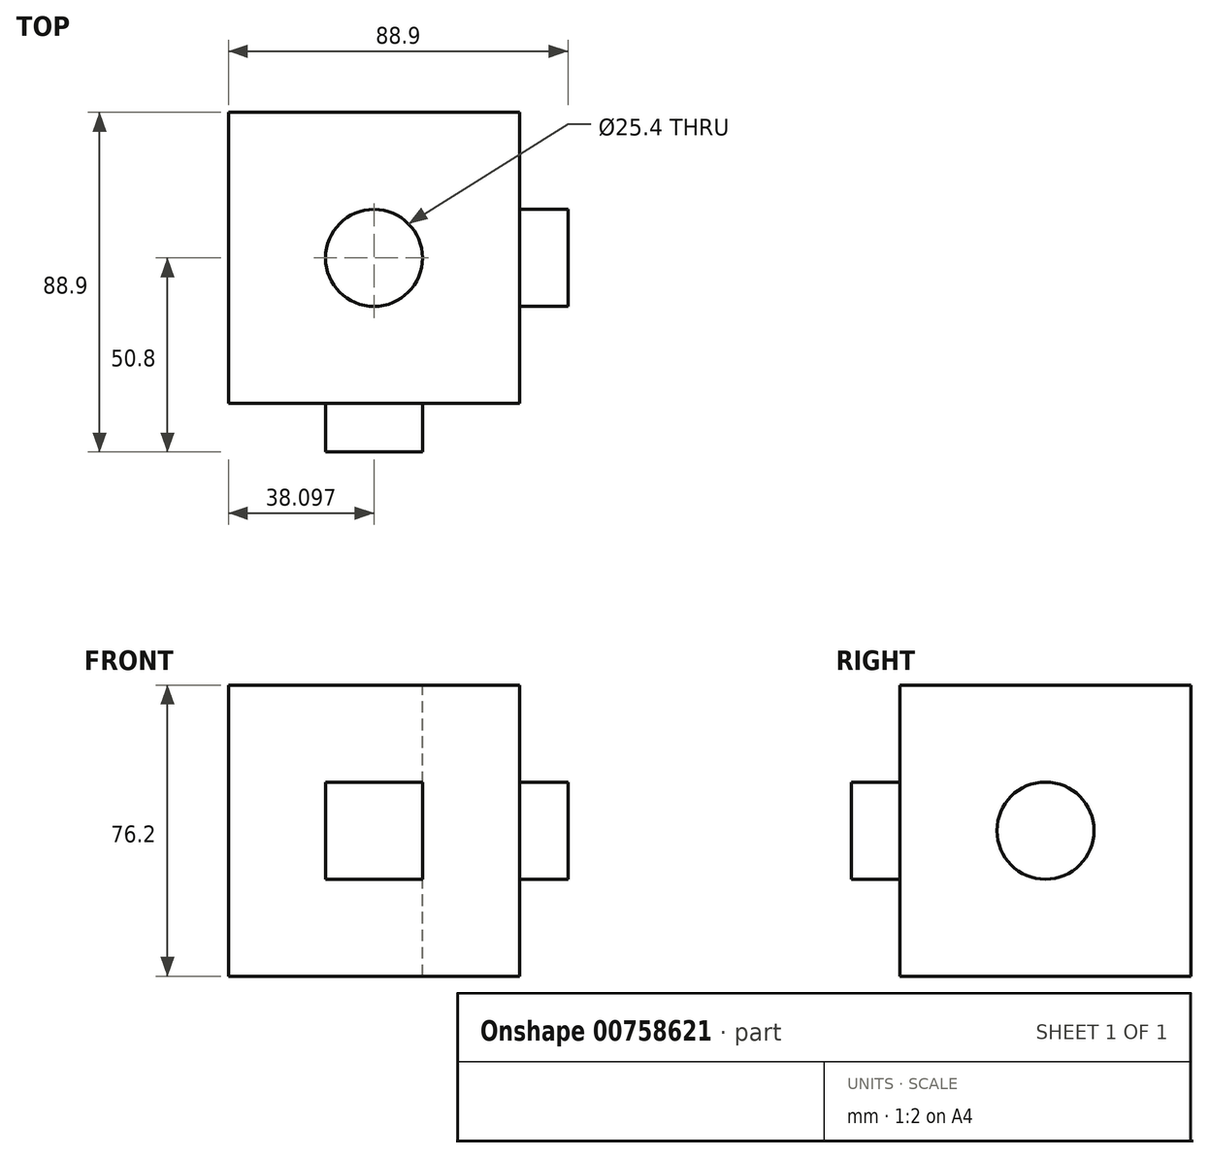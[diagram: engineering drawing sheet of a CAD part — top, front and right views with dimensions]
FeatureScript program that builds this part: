
annotation { "Feature Type Name" : "Feature", "Feature Type Description" : "" }
export const myFeature = defineFeature(function(context is Context, id is Id, definition is map)
    precondition{}
    {
        {
            var Q0;
            Q0=qCreatedBy(makeId("Front.planeOp"),FACE);
            var sketch = newSketch(context, id + "F0", { "sketchPlane" : qUnion([Q0])});
            skLineSegment(sketch, "E0.bottom", {"start": v(-44.43, 31.42) * mm, "end": v(31.77, 31.42) * mm});
            skLineSegment(sketch, "E0.top", {"start": v(-44.43, -44.78) * mm, "end": v(31.77, -44.78) * mm});
            skLineSegment(sketch, "E0.left", {"start": v(-44.43, 31.42) * mm, "end": v(-44.43, -44.78) * mm});
            skLineSegment(sketch, "E0.right", {"start": v(31.77, 31.42) * mm, "end": v(31.77, -44.78) * mm});
            skSolve(sketch);
        }
        {
            var Q0;
            Q0=makeQuery(id+"F0.imprint","IMPRINT",FACE,{"disambiguationData":[TD([[makeQuery(id+"F0.imprint","IMPRINT",EDGE,{"derivedFrom":sQuery(id+"F0.wireOp",EDGE,"E0.bottom")}),-1.0]])]});
            extrude(context, id + "F1", {"entities" : qUnion([Q0]), "depth" : 76.2 * mm, "offsetDistance" : 25.4 * mm});
        }
        {
            var Q0;
            Q0=makeQuery(id+"F1.opExtrude","CAP_FACE",FACE,{"disambiguationData":[OSD([sQuery(id+"F0.wireOp",EDGE,"E0.bottom"),sQuery(id+"F0.wireOp",EDGE,"E0.top"),sQuery(id+"F0.wireOp",EDGE,"E0.left"),sQuery(id+"F0.wireOp",EDGE,"E0.right")])],"isStart":false});
            var sketch = newSketch(context, id + "F2", { "sketchPlane" : qUnion([Q0])});
            skLineSegment(sketch, "E1.bottom", {"start": v(-19.03, -19.38) * mm, "end": v(6.37, -19.38) * mm});
            skLineSegment(sketch, "E1.top", {"start": v(-19.03, 6.02) * mm, "end": v(6.37, 6.02) * mm});
            skLineSegment(sketch, "E1.left", {"start": v(-19.03, -19.38) * mm, "end": v(-19.03, 6.02) * mm});
            skLineSegment(sketch, "E1.right", {"start": v(6.37, -19.38) * mm, "end": v(6.37, 6.02) * mm});
            skSolve(sketch);
        }
        {
            var Q0;
            Q0=makeQuery(id+"F2.imprint","IMPRINT",FACE,{"disambiguationData":[TD([[makeQuery(id+"F2.imprint","IMPRINT",EDGE,{"derivedFrom":sQuery(id+"F2.wireOp",EDGE,"E1.bottom")}),1.0]])]});
            extrude(context, id + "F3", {"entities" : qUnion([Q0]), "operationType" : NewBodyOperationType.ADD, "depth" : 12.7 * mm, "offsetDistance" : 25.4 * mm});
        }
        {
            var Q0;
            Q0=makeQuery(id+"F1.opExtrude","SWEPT_FACE",FACE,{"disambiguationData":[OSD([sQuery(id+"F0.wireOp",EDGE,"E0.right")])]});
            var sketch = newSketch(context, id + "F4", { "sketchPlane" : qUnion([Q0])});
            skCircle(sketch, "E2", {"center": v(-38.1, -6.68) * mm, "radius": 12.7 * mm});
            skSolve(sketch);
        }
        {
            var Q0;
            Q0 = qSketchRegion(id + "F4", true);
            extrude(context, id + "F5", {"entities" : qUnion([Q0]), "operationType" : NewBodyOperationType.ADD, "depth" : 12.7 * mm, "offsetDistance" : 25.4 * mm});
        }
        {
            var Q0;
            Q0=makeQuery(id+"F1.opExtrude","SWEPT_FACE",FACE,{"disambiguationData":[OSD([sQuery(id+"F0.wireOp",EDGE,"E0.bottom")])]});
            var sketch = newSketch(context, id + "F6", { "sketchPlane" : qUnion([Q0])});
            skPoint(sketch, "E3", {"position": v(-6.33, -38.1) * mm});
            skSolve(sketch);
        }
        {
            var Q0;
            Q0=sQuery(id+"F6.wireOp",VERTEX,"E3");
            var Q1;
            Q1=makeQuery(id+"F1.opExtrude","SWEPT_BODY",BODY,{"disambiguationData":[OSD([sQuery(id+"F0.wireOp",EDGE,"E0.bottom"),sQuery(id+"F0.wireOp",EDGE,"E0.top"),sQuery(id+"F0.wireOp",EDGE,"E0.left"),sQuery(id+"F0.wireOp",EDGE,"E0.right")])]});
            hole(context, id + "F7", {"style" : HoleStyle.SIMPLE, "endStyle" : HoleEndStyle.THROUGH, "holeDiameter" : 25.4 * mm, "majorDiameter" : 6.35 * mm, "isTappedThrough" : true, "tappedDepth" : 12.7 * mm, "tapClearance" : 3, "locations" : qUnion([Q0]), "scope" : qUnion([Q1])});
        }
    });
